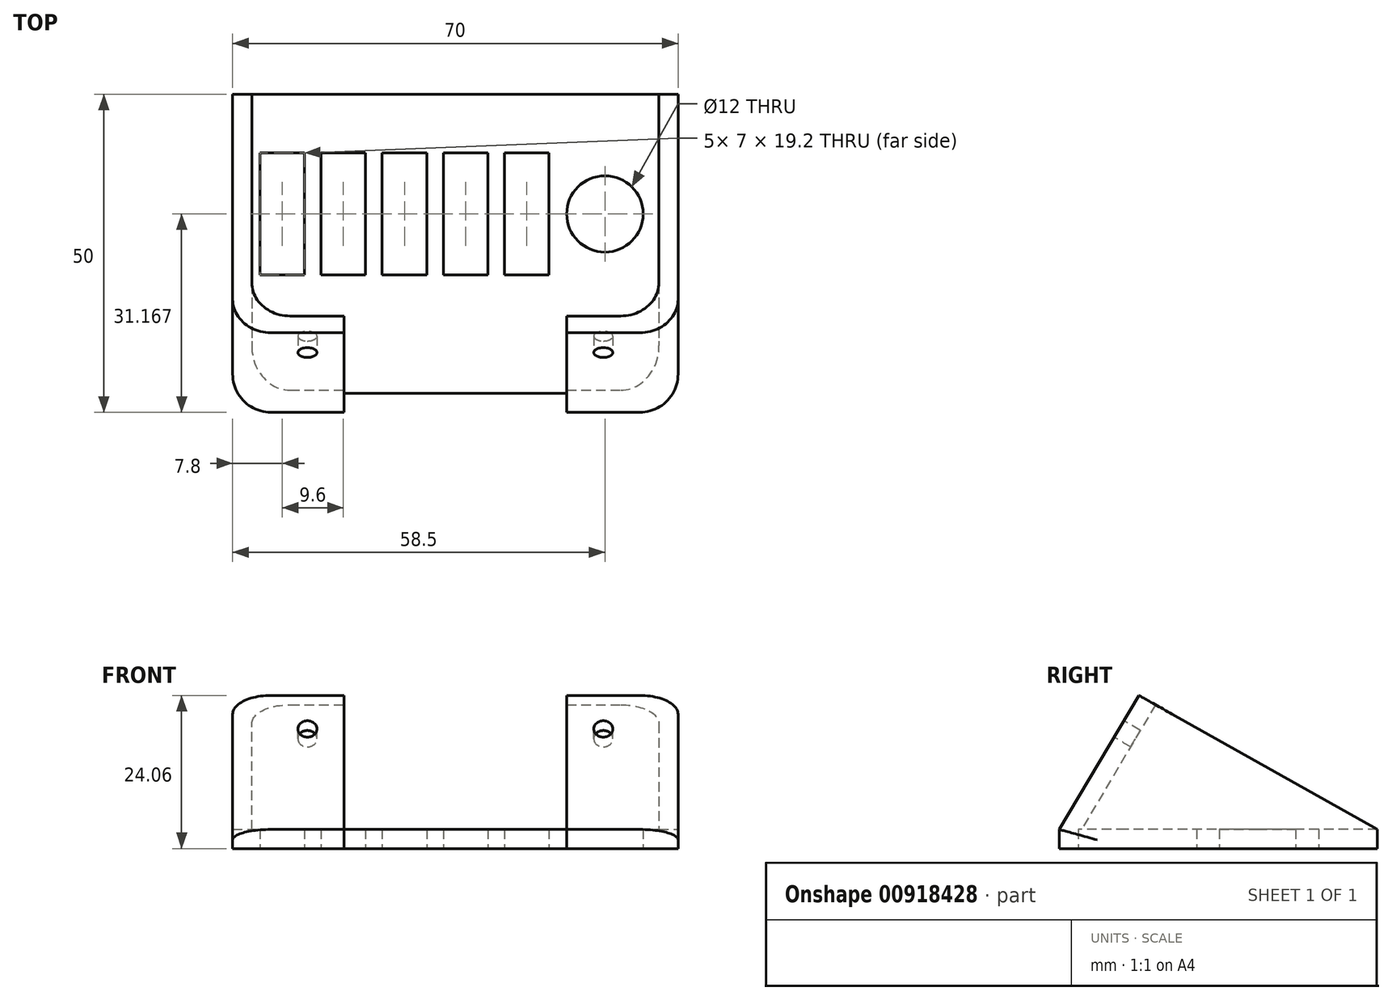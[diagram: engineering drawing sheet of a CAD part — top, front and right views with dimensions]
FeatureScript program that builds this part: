
annotation { "Feature Type Name" : "Feature", "Feature Type Description" : "" }
export const myFeature = defineFeature(function(context is Context, id is Id, definition is map)
    precondition{}
    {
        {
            assignVariable(context, id + "F0", {"name" : "MountWidth", "anyValue" : 70});
        }
        {
            assignVariable(context, id + "F1", {"name" : "WallThickness", "anyValue" : 3});
        }
        {
            assignVariable(context, id + "F2", {"name" : "WireGap", "anyValue" : 35});
        }
        {
            var Q0;
            Q0=qCreatedBy(makeId("Top.planeOp"),FACE);
            var sketch = newSketch(context, id + "F3", { "sketchPlane" : qUnion([Q0])});
            skLineSegment(sketch, "E0.bottom", {"start": v(-35, 25) * mm, "end": v(35, 25) * mm});
            skLineSegment(sketch, "E0.top", {"start": v(-35, -25) * mm, "end": v(-17.5, -25) * mm});
            skLineSegment(sketch, "E0.left", {"start": v(-35, 25) * mm, "end": v(-35, -25) * mm});
            skLineSegment(sketch, "E0.right", {"start": v(35, 25) * mm, "end": v(35, -25) * mm});
            skLineSegment(sketch, "E1", {"start": v(-35, 16.67) * mm, "end": v(35, 16.67) * mm, "construction": true});
            skLineSegment(sketch, "E2", {"start": v(-35, -4.33) * mm, "end": v(35, -4.33) * mm, "construction": true});
            skPoint(sketch, "E2.endSnap0", {"position": v(35, 0) * mm});
            skLineSegment(sketch, "E3", {"start": v(-35, 15.77) * mm, "end": v(35, 15.77) * mm, "construction": true});
            skLineSegment(sketch, "E4", {"start": v(-35, -3.43) * mm, "end": v(35, -3.43) * mm, "construction": true});
            skPoint(sketch, "E5", {"position": v(0, 25) * mm});
            skLineSegment(sketch, "E6.bottom", {"start": v(-30.7, 15.77) * mm, "end": v(-23.7, 15.77) * mm});
            skLineSegment(sketch, "E6.top", {"start": v(-30.7, -3.43) * mm, "end": v(-23.7, -3.43) * mm});
            skLineSegment(sketch, "E6.left", {"start": v(-30.7, 15.77) * mm, "end": v(-30.7, -3.43) * mm});
            skLineSegment(sketch, "E6.right", {"start": v(-23.7, 15.77) * mm, "end": v(-23.7, -3.43) * mm});
            skLineSegment(sketch, "E7.bottom", {"start": v(-21.1, 15.77) * mm, "end": v(-14.1, 15.77) * mm});
            skLineSegment(sketch, "E7.top", {"start": v(-21.1, -3.43) * mm, "end": v(-14.1, -3.43) * mm});
            skLineSegment(sketch, "E7.left", {"start": v(-21.1, 15.77) * mm, "end": v(-21.1, -3.43) * mm});
            skLineSegment(sketch, "E7.right", {"start": v(-14.1, 15.77) * mm, "end": v(-14.1, -3.43) * mm});
            skLineSegment(sketch, "E8.bottom", {"start": v(-11.5, 15.77) * mm, "end": v(-4.5, 15.77) * mm});
            skLineSegment(sketch, "E8.top", {"start": v(-11.5, -3.43) * mm, "end": v(-4.5, -3.43) * mm});
            skLineSegment(sketch, "E8.left", {"start": v(-11.5, 15.77) * mm, "end": v(-11.5, -3.43) * mm});
            skLineSegment(sketch, "E8.right", {"start": v(-4.5, 15.77) * mm, "end": v(-4.5, -3.43) * mm});
            skLineSegment(sketch, "E9.bottom", {"start": v(-1.9, 15.77) * mm, "end": v(5.1, 15.77) * mm});
            skLineSegment(sketch, "E9.top", {"start": v(-1.9, -3.43) * mm, "end": v(5.1, -3.43) * mm});
            skLineSegment(sketch, "E9.left", {"start": v(-1.9, 15.77) * mm, "end": v(-1.9, -3.43) * mm});
            skLineSegment(sketch, "E9.right", {"start": v(5.1, 15.77) * mm, "end": v(5.1, -3.43) * mm});
            skLineSegment(sketch, "E10.bottom", {"start": v(7.7, 15.77) * mm, "end": v(14.7, 15.77) * mm});
            skLineSegment(sketch, "E10.top", {"start": v(7.7, -3.43) * mm, "end": v(14.7, -3.43) * mm});
            skLineSegment(sketch, "E10.left", {"start": v(7.7, 15.77) * mm, "end": v(7.7, -3.43) * mm});
            skLineSegment(sketch, "E10.right", {"start": v(14.7, 15.77) * mm, "end": v(14.7, -3.43) * mm});
            skCircle(sketch, "E11", {"center": v(23.5, 6.17) * mm, "radius": 6 * mm});
            skPoint(sketch, "E12", {"position": v(14.7, 6.17) * mm});
            skLineSegment(sketch, "E13", {"start": v(14.7, 6.17) * mm, "end": v(35, 6.17) * mm, "construction": true});
            skLineSegment(sketch, "E14", {"start": v(-17.5, -25) * mm, "end": v(-17.5, -22) * mm});
            skLineSegment(sketch, "E15", {"start": v(-17.5, -22) * mm, "end": v(17.5, -22) * mm});
            skLineSegment(sketch, "E16", {"start": v(17.5, -22) * mm, "end": v(17.5, -25) * mm});
            skPoint(sketch, "E17", {"position": v(0, -22) * mm});
            skLineSegment(sketch, "E18.trimOffspring", {"start": v(17.5, -25) * mm, "end": v(35, -25) * mm});
            skCircle(sketch, "E19", {"center": v(23.5, 6.17) * mm, "radius": 7.5 * mm, "construction": true});
            skSolve(sketch);
        }
        {
            var Q0;
            {var subQ1=sQuery(id+"F3.wireOp",EDGE,"E0.bottom");Q0=makeQuery(id+"F3.imprint","IMPRINT",FACE,{"disambiguationData":[TD([[makeQuery(id+"F3.imprint","IMPRINT",EDGE,{"derivedFrom":subQ1}),-1.0]])]});}
            extrude(context, id + "F4", {"entities" : qUnion([Q0]), "depth" : (getVariable(context, 'WallThickness')) * mm, "offsetDistance" : 25 * mm});
        }
        {
            var Q0;
            {var subQ0=sQuery(id+"F3.wireOp",EDGE,"E0.right");Q0=makeQuery(id+"F4.boolean.opBoolean","MERGE",FACE,{"derivedFrom":[makeQuery(id+"FGnrFPLAvgotBto_0.opExtrude","SWEPT_FACE",FACE,{"disambiguationData":[OSD([subQ0])]}),makeQuery(id+"F4.opExtrude","SWEPT_FACE",FACE,{"disambiguationData":[OSD([subQ0])]})]});}
            cPlane(context, id + "F5", {"entities" : qUnion([Q0]), "cplaneType" : CPlaneType.OFFSET, "offset" : 0 * mm, "width" : 150 * mm, "height" : 150 * mm});
        }
        {
            var Q0;
            Q0=qCreatedBy(id+"F5.planeOp",FACE);
            var sketch = newSketch(context, id + "F6", { "sketchPlane" : qUnion([Q0])});
            skLineSegment(sketch, "E20", {"start": v(-25, 3) * mm, "end": v(-12.49, 24.06) * mm});
            skLineSegment(sketch, "E21", {"start": v(25, 3) * mm, "end": v(-12.49, 24.06) * mm});
            skLineSegment(sketch, "E22.0", {"start": v(25, 3) * mm, "end": v(25, 3) * mm});
            skLineSegment(sketch, "E23", {"start": v(-9.87, 22.6) * mm, "end": v(-21.51, 3) * mm});
            skLineSegment(sketch, "E24.0", {"start": v(25, 3) * mm, "end": v(-25, 3) * mm});
            skSolve(sketch);
        }
        {
            var Q0;
            {var subQ0=sQuery(id+"F6.wireOp",EDGE,"E20");Q0=makeQuery(id+"F6.imprint","IMPRINT",FACE,{"disambiguationData":[TD([[makeQuery(id+"F6.imprint","IMPRINT",EDGE,{"derivedFrom":subQ0}),-1.0]])]});}
            var Q1;
            {var subQ3=sQuery(id+"F6.wireOp",EDGE,"E23");Q1=makeQuery(id+"F6.imprint","IMPRINT",FACE,{"disambiguationData":[TD([[makeQuery(id+"F6.imprint","IMPRINT",EDGE,{"derivedFrom":subQ3}),1.0]])]});}
            extrude(context, id + "F7", {"entities" : qUnion([Q0, Q1]), "operationType" : NewBodyOperationType.ADD, "oppositeDirection" : true, "depth" : (getVariable(context, 'WallThickness')) * mm, "offsetDistance" : 25 * mm});
        }
        {
            var Q0;
            {var subQ0=sQuery(id+"F6.wireOp",EDGE,"E20");Q0=makeQuery(id+"F6.imprint","IMPRINT",FACE,{"disambiguationData":[TD([[makeQuery(id+"F6.imprint","IMPRINT",EDGE,{"derivedFrom":subQ0}),-1.0]])]});}
            var Q1;
            {var subQ3=sQuery(id+"F6.wireOp",EDGE,"E23");Q1=makeQuery(id+"F6.imprint","IMPRINT",FACE,{"disambiguationData":[TD([[makeQuery(id+"F6.imprint","IMPRINT",EDGE,{"derivedFrom":subQ3}),1.0]])]});}
            extrude(context, id + "F8", {"entities" : qUnion([Q0, Q1]), "operationType" : NewBodyOperationType.ADD, "oppositeDirection" : true, "depth" : (getVariable(context, 'MountWidth')) * mm, "offsetDistance" : 25 * mm, "hasSecondDirection" : true, "secondDirectionOppositeDirection" : true, "secondDirectionDepth" : (getVariable(context, 'MountWidth') - getVariable(context, 'WallThickness')) * mm});
        }
        {
            var Q0;
            {var subQ0=sQuery(id+"F6.wireOp",EDGE,"E20");Q0=makeQuery(id+"F6.imprint","IMPRINT",FACE,{"disambiguationData":[TD([[makeQuery(id+"F6.imprint","IMPRINT",EDGE,{"derivedFrom":subQ0}),-1.0]])]});}
            extrude(context, id + "F9", {"entities" : qUnion([Q0]), "operationType" : NewBodyOperationType.ADD, "oppositeDirection" : true, "depth" : (getVariable(context, 'MountWidth')) * mm, "offsetDistance" : 25 * mm, "hasSecondDirection" : true, "secondDirectionOppositeDirection" : true, "secondDirectionDepth" : ((getVariable(context, 'MountWidth') + getVariable(context, 'WireGap')) / 2) * mm});
        }
        {
            var Q0;
            {var subQ0=sQuery(id+"F6.wireOp",EDGE,"E20");Q0=makeQuery(id+"F6.imprint","IMPRINT",FACE,{"disambiguationData":[TD([[makeQuery(id+"F6.imprint","IMPRINT",EDGE,{"derivedFrom":subQ0}),-1.0]])]});}
            extrude(context, id + "F10", {"entities" : qUnion([Q0]), "operationType" : NewBodyOperationType.ADD, "oppositeDirection" : true, "depth" : ((getVariable(context, 'MountWidth') - getVariable(context, 'WireGap')) / 2) * mm, "offsetDistance" : 25 * mm});
        }
        {
            var Q0;
            Q0=makeQuery(id+"F10.boolean.opBoolean","INTERSECT",EDGE,{"derivedFrom":[makeQuery(id+"F7.opExtrude","CAP_FACE",FACE,{"disambiguationData":[OSD([sQuery(id+"F6.wireOp",EDGE,"E20"),sQuery(id+"F6.wireOp",EDGE,"E21"),sQuery(id+"F6.wireOp",EDGE,"E24.0")])],"isStart":false}),makeQuery(id+"F10.opExtrude","SWEPT_FACE",FACE,{"disambiguationData":[OSD([sQuery(id+"F6.wireOp",EDGE,"E23")])]})]});
            var Q1;
            Q1=makeQuery(id+"F9.boolean.opBoolean","INTERSECT",EDGE,{"derivedFrom":[makeQuery(id+"F8.opExtrude","CAP_FACE",FACE,{"disambiguationData":[OSD([sQuery(id+"F6.wireOp",EDGE,"E20"),sQuery(id+"F6.wireOp",EDGE,"E21"),sQuery(id+"F6.wireOp",EDGE,"E24.0")])],"isStart":true}),makeQuery(id+"F9.opExtrude","SWEPT_FACE",FACE,{"disambiguationData":[OSD([sQuery(id+"F6.wireOp",EDGE,"E23")])]})]});
            var Q2;
            Q2=makeQuery(id+"F9.opExtrude","SWEPT_EDGE",EDGE,{"disambiguationData":[OSD([sQuery(id+"F6.wireOp",EDGE,"E23"),sQuery(id+"F6.wireOp",EDGE,"E24.0")])]});
            var Q3;
            Q3=makeQuery(id+"F10.opExtrude","SWEPT_EDGE",EDGE,{"disambiguationData":[OSD([sQuery(id+"F6.wireOp",EDGE,"E23"),sQuery(id+"F6.wireOp",EDGE,"E24.0")])]});
            var Q4;
            Q4=makeQuery(id+"F7.opExtrude","CAP_EDGE",EDGE,{"disambiguationData":[OSD([sQuery(id+"F6.wireOp",EDGE,"E20")])],"isStart":true});
            var Q5;
            Q5=makeQuery(id+"F8.opExtrude","CAP_EDGE",EDGE,{"disambiguationData":[OSD([sQuery(id+"F6.wireOp",EDGE,"E20")])],"isStart":false});
            var Q6;
            Q6=makeQuery(id+"F4.opExtrude","SWEPT_EDGE",EDGE,{"disambiguationData":[OSD([sQuery(id+"F3.wireOp",EDGE,"E0.top"),sQuery(id+"F3.wireOp",EDGE,"E0.left")])]});
            var Q7;
            Q7=makeQuery(id+"F4.opExtrude","SWEPT_EDGE",EDGE,{"disambiguationData":[OSD([sQuery(id+"F3.wireOp",EDGE,"E0.right"),sQuery(id+"F3.wireOp",EDGE,"E18.trimOffspring")])]});
            fillet(context, id + "F11", {"entities" : qUnion([Q0, Q1, Q2, Q3, Q4, Q5, Q6, Q7]), "radius" : 6 * mm, "tangentPropagation" : true, "allowEdgeOverflow" : false});
        }
        {
            var Q0;
            {var subQ0=sQuery(id+"F6.wireOp",EDGE,"E20");Q0=makeQuery(id+"F9.boolean.opBoolean","MERGE",FACE,{"derivedFrom":[makeQuery(id+"F8.opExtrude","SWEPT_FACE",FACE,{"disambiguationData":[OSD([subQ0])]}),makeQuery(id+"F9.opExtrude","SWEPT_FACE",FACE,{"disambiguationData":[OSD([subQ0])]})]});}
            cPlane(context, id + "F12", {"entities" : qUnion([Q0]), "cplaneType" : CPlaneType.OFFSET, "offset" : 0 * mm, "width" : 150 * mm, "height" : 150 * mm});
        }
        {
            var Q0;
            Q0=qCreatedBy(id+"F12.planeOp",FACE);
            var sketch = newSketch(context, id + "F13", { "sketchPlane" : qUnion([Q0])});
            skLineSegment(sketch, "E25.0", {"start": v(-29, 14.31) * mm, "end": v(-29, -10.19) * mm});
            skLineSegment(sketch, "E26.0", {"start": v(29, -10.19) * mm, "end": v(29, 14.31) * mm});
            skLineSegment(sketch, "E27.0", {"start": v(17.5, -10.19) * mm, "end": v(17.5, 14.31) * mm});
            skLineSegment(sketch, "E28.0", {"start": v(-17.5, -10.19) * mm, "end": v(-17.5, 14.31) * mm});
            skPoint(sketch, "E29", {"position": v(-17.5, 2.06) * mm});
            skPoint(sketch, "E30", {"position": v(-29, 2.06) * mm});
            skPoint(sketch, "E31", {"position": v(17.5, 2.06) * mm});
            skPoint(sketch, "E32", {"position": v(29, 2.06) * mm});
            skCircle(sketch, "E33", {"center": v(-23.25, 8.19) * mm, "radius": 1.5 * mm});
            skCircle(sketch, "E34", {"center": v(23.25, 8.19) * mm, "radius": 1.5 * mm});
            skLineSegment(sketch, "E35", {"start": v(-29, 14.31) * mm, "end": v(-17.5, 2.06) * mm, "construction": true});
            skLineSegment(sketch, "E36", {"start": v(-29, 2.06) * mm, "end": v(-17.5, 14.31) * mm, "construction": true});
            skLineSegment(sketch, "E37", {"start": v(17.5, 2.06) * mm, "end": v(29, 14.31) * mm, "construction": true});
            skLineSegment(sketch, "E38", {"start": v(29, 2.06) * mm, "end": v(17.5, 14.31) * mm, "construction": true});
            skSolve(sketch);
        }
        {
            var Q0;
            Q0=makeQuery(id+"F13.imprint","IMPRINT",FACE,{"disambiguationData":[TD([[makeQuery(id+"F13.imprint","IMPRINT",EDGE,{"derivedFrom":sQuery(id+"F13.wireOp",EDGE,"E33")}),1.0]])]});
            var Q1;
            Q1=makeQuery(id+"F13.imprint","IMPRINT",FACE,{"disambiguationData":[TD([[makeQuery(id+"F13.imprint","IMPRINT",EDGE,{"derivedFrom":sQuery(id+"F13.wireOp",EDGE,"E34")}),1.0]])]});
            extrude(context, id + "F14", {"entities" : qUnion([Q0, Q1]), "operationType" : NewBodyOperationType.REMOVE, "oppositeDirection" : true, "depth" : 5 * mm, "offsetDistance" : 25 * mm});
        }
    });
